# Revit family: M02
name_source: partatom
category: Verbindungsmittel
units: mm (PartAtom-declared; Revit-internal decimal feet)

## family parameters
Arbeitsebenenbasiert = Nein
Beim Laden mit Abzugskörper schneiden = Nein
Gemeinsam genutzt = Nein
Immer vertikal = Nein
OmniClass-Nummer = 23.25.10.27.11.21
OmniClass-Titel = Reinforcement Couplers

## types (9) — shared parameters
Endenbearbeitung 1 = Mit Gewinde
Endenbearbeitung 2 = Mit Gewinde
Hersteller = Stahlwerk Annahütte Max Aicher GmbH Co.KG
M02_Vis = Ja
Typenbild = M02.png
Typenkommentare = M02-Muffenstoß
URL = http//:www.annahuette.com

## per-type parameters (varying)
- M02-ø22/18: Außendurchmesser=40 mm  [stored 0.131234 ft]; Beschreibung=M02-ø22/8; Einfassung Stab 1=55 mm  [stored 0.180446 ft]; Einfassung Stab 2=50 mm  [stored 0.164042 ft]; Gesamtlänge=175 mm; Körper=1,00 kg; M03-Gewicht=1,22 kg; Modell=M02=TR 3102+TR2040; Nenndurchmesser_01 ø=22 mm  [stored 0.0721785 ft]; Nenndurchmesser_02 ø=18 mm  [stored 0.0590551 ft]; Pos_TR2040_01=95 mm; Pos_TR2040_02=95 mm; Pos_TR3102=73 mm; Stabgröße 1=SAS 670 - ø22; Stabgröße 2=SAS 670 - ø18; TR2040-G01=0,12 kg; TR2040-G02=0,10 kg; TR2040-L01=22 mm  [stored 0.0721785 ft]; TR2040-L02=22 mm  [stored 0.0721785 ft]; TR2040-Sw01=36 mm  [stored 0.11811 ft]; TR2040_Sw02=30 mm  [stored 0.0984252 ft]; TR3102-L=145 mm  [stored 0.475722 ft]; TR3102-L1=55 mm  [stored 0.180446 ft]; TR3102-L2=50 mm  [stored 0.164042 ft]; TR3102-d=40 mm  [stored 0.131234 ft]
- M02-ø25/22: Außendurchmesser=45 mm  [stored 0.147638 ft]; Beschreibung=M02-ø25/22; Einfassung Stab 1=60 mm  [stored 0.19685 ft]; Einfassung Stab 2=55 mm  [stored 0.180446 ft]; Gesamtlänge=190 mm; Körper=1,40 kg; M03-Gewicht=1,68 kg; Modell=M02=TR 3102+TR2040; Nenndurchmesser_01 ø=25 mm  [stored 0.082021 ft]; Nenndurchmesser_02 ø=22 mm  [stored 0.0721785 ft]; Pos_TR2040_01=102 mm  [stored 0.334646 ft]; Pos_TR2040_02=102 mm  [stored 0.334646 ft]; Pos_TR3102=80 mm  [stored 0.262467 ft]; Stabgröße 1=SAS 670 - ø25; Stabgröße 2=SAS 670 - ø22; TR2040-G01=0,16 kg; TR2040-G02=0,12 kg; TR2040-L01=22 mm  [stored 0.0721785 ft]; TR2040-L02=22 mm  [stored 0.0721785 ft]; TR2040-Sw01=41 mm  [stored 0.134514 ft]; TR2040_Sw02=36 mm  [stored 0.11811 ft]; TR3102-L=160 mm; TR3102-L1=60 mm  [stored 0.19685 ft]; TR3102-L2=55 mm  [stored 0.180446 ft]; TR3102-d=45 mm  [stored 0.147638 ft]
- M02-ø28/25: Außendurchmesser=50 mm  [stored 0.164042 ft]; Beschreibung=M02-ø28/25; Einfassung Stab 1=70 mm  [stored 0.229659 ft]; Einfassung Stab 2=60 mm  [stored 0.19685 ft]; Gesamtlänge=205 mm; Körper=2,00 kg; M03-Gewicht=2,42 kg; Modell=M02=TR 3102+TR2040; Nenndurchmesser_01 ø=28 mm  [stored 0.0918635 ft]; Nenndurchmesser_02 ø=25 mm  [stored 0.082021 ft]; Pos_TR2040_01=120 mm  [stored 0.393701 ft]; Pos_TR2040_02=112 mm; Pos_TR3102=90 mm  [stored 0.295276 ft]; Stabgröße 1=SAS 670 - ø28; Stabgröße 2=SAS 670 - ø25; TR2040-G01=0,26 kg; TR2040-G02=0,16 kg; TR2040-L01=30 mm  [stored 0.0984252 ft]; TR2040-L02=22 mm  [stored 0.0721785 ft]; TR2040-Sw01=46 mm  [stored 0.150919 ft]; TR2040_Sw02=41 mm  [stored 0.134514 ft]; TR3102-L=180 mm; TR3102-L1=70 mm  [stored 0.229659 ft]; TR3102-L2=60 mm  [stored 0.19685 ft]; TR3102-d=50 mm  [stored 0.164042 ft]
- M02-ø30/28: Außendurchmesser=55 mm  [stored 0.180446 ft]; Beschreibung=M02-ø30/28; Einfassung Stab 1=75 mm; Einfassung Stab 2=70 mm  [stored 0.229659 ft]; Gesamtlänge=225 mm; Körper=2,50 kg; M03-Gewicht=3,07 kg; Modell=M02=TR 3102+TR2040; Nenndurchmesser_01 ø=30 mm  [stored 0.0984252 ft]; Nenndurchmesser_02 ø=28 mm  [stored 0.0918635 ft]; Pos_TR2040_01=128 mm; Pos_TR2040_02=128 mm; Pos_TR3102=98 mm; Stabgröße 1=SAS 670 - ø30; Stabgröße 2=SAS 670 - ø28; TR2040-G01=0,31 kg; TR2040-G02=0,26 kg; TR2040-L01=30 mm  [stored 0.0984252 ft]; TR2040-L02=30 mm  [stored 0.0984252 ft]; TR2040-Sw01=50 mm  [stored 0.164042 ft]; TR2040_Sw02=46 mm  [stored 0.150919 ft]; TR3102-L=195 mm; TR3102-L1=75 mm; TR3102-L2=70 mm  [stored 0.229659 ft]; TR3102-d=55 mm  [stored 0.180446 ft]
- M02-ø35/30: Außendurchmesser=60 mm  [stored 0.19685 ft]; Beschreibung=M02-ø35/30; Einfassung Stab 1=85 mm  [stored 0.278871 ft]; Einfassung Stab 2=75 mm; Gesamtlänge=260 mm; Körper=3,00 kg; M03-Gewicht=3,78 kg; Modell=M02=TR 3102+TR2040; Nenndurchmesser_01 ø=35 mm  [stored 0.114829 ft]; Nenndurchmesser_02 ø=30 mm  [stored 0.0984252 ft]; Pos_TR2040_01=148 mm; Pos_TR2040_02=138 mm; Pos_TR3102=108 mm; Stabgröße 1=SAS 670 - ø35; Stabgröße 2=SAS 670 - ø30; TR2040-G01=0,47 kg; TR2040-G02=0,31 kg; TR2040-L01=40 mm  [stored 0.131234 ft]; TR2040-L02=30 mm  [stored 0.0984252 ft]; TR2040-Sw01=55 mm  [stored 0.180446 ft]; TR2040_Sw02=50 mm  [stored 0.164042 ft]; TR3102-L=215 mm; TR3102-L1=85 mm  [stored 0.278871 ft]; TR3102-L2=75 mm; TR3102-d=60 mm  [stored 0.19685 ft]
- M02-ø43/35: Außendurchmesser=80 mm  [stored 0.262467 ft]; Beschreibung=M02-ø43/35; Einfassung Stab 1=100 mm  [stored 0.328084 ft]; Einfassung Stab 2=85 mm  [stored 0.278871 ft]; Gesamtlänge=275 mm; Körper=5,50 kg; M03-Gewicht=6,97 kg; Modell=M02=TR 3102+TR2040; Nenndurchmesser_01 ø=43 mm  [stored 0.141076 ft]; Nenndurchmesser_02 ø=35 mm  [stored 0.114829 ft]; Pos_TR2040_01=175 mm; Pos_TR2040_02=165 mm; Pos_TR3102=125 mm  [stored 0.410105 ft]; Stabgröße 1=SAS 670 - ø43; Stabgröße 2=SAS 670 - ø35; TR2040-G01=1,00 kg; TR2040-G02=0,47 kg; TR2040-L01=50 mm  [stored 0.164042 ft]; TR2040-L02=40 mm  [stored 0.131234 ft]; TR2040-Sw01=70 mm  [stored 0.229659 ft]; TR2040_Sw02=55 mm  [stored 0.180446 ft]; TR3102-L=250 mm; TR3102-L1=100 mm  [stored 0.328084 ft]; TR3102-L2=85 mm  [stored 0.278871 ft]; TR3102-d=80 mm  [stored 0.262467 ft]
- M02-ø50/43: Außendurchmesser=85 mm  [stored 0.278871 ft]; Beschreibung=M02-ø50/43; Einfassung Stab 1=105 mm  [stored 0.344488 ft]; Einfassung Stab 2=100 mm  [stored 0.328084 ft]; Gesamtlänge=335 mm; Körper=7,68 kg; M03-Gewicht=9,94 kg; Modell=M02=TR3102+TR2040; Nenndurchmesser_01 ø=50 mm  [stored 0.164042 ft]; Nenndurchmesser_02 ø=43 mm  [stored 0.141076 ft]; Pos_TR2040_01=185 mm; Pos_TR2040_02=185 mm; Pos_TR3102=135 mm  [stored 0.442913 ft]; Stabgröße 1=SAS 670 - ø50; Stabgröße 2=SAS 670 - ø43; TR2040-G01=1,26 kg; TR2040-G02=1,00 kg; TR2040-L01=50 mm  [stored 0.164042 ft]; TR2040-L02=50 mm  [stored 0.164042 ft]; TR2040-Sw01=80 mm  [stored 0.262467 ft]; TR2040_Sw02=70 mm  [stored 0.229659 ft]; TR3102-L=270 mm; TR3102-L1=105 mm  [stored 0.344488 ft]; TR3102-L2=100 mm  [stored 0.328084 ft]; TR3102-d=85 mm  [stored 0.278871 ft]
- M02-ø57,5/50: Außendurchmesser=100 mm  [stored 0.328084 ft]; Beschreibung=M02-ø57,5/50; Einfassung Stab 1=125 mm  [stored 0.410105 ft]; Einfassung Stab 2=105 mm  [stored 0.344488 ft]; Gesamtlänge=350 mm; Körper=11,94 kg; M03-Gewicht=15,24 kg; Modell=M02=TR 3102+TR2040; Nenndurchmesser_01 ø=58 mm; Nenndurchmesser_02 ø=50 mm  [stored 0.164042 ft]; Pos_TR2040_01=208 mm; Pos_TR2040_02=198 mm; Pos_TR3102=148 mm; Stabgröße 1=SAS 670 - ø57,5; Stabgröße 2=SAS 670 - ø50; TR2040-G01=2,04 kg; TR2040-G02=1,26 kg; TR2040-L01=60 mm  [stored 0.19685 ft]; TR2040-L02=50 mm  [stored 0.164042 ft]; TR2040-Sw01=90 mm  [stored 0.295276 ft]; TR2040_Sw02=80 mm  [stored 0.262467 ft]; TR3102-L=295 mm; TR3102-L1=125 mm  [stored 0.410105 ft]; TR3102-L2=105 mm  [stored 0.344488 ft]; TR3102-d=100 mm  [stored 0.328084 ft]
- M02-ø63,5/57,5: Außendurchmesser=110 mm  [stored 0.360892 ft]; Beschreibung=M02-ø63,5/57,5; Einfassung Stab 1=130 mm  [stored 0.426509 ft]; Einfassung Stab 2=125 mm  [stored 0.410105 ft]; Gesamtlänge=405 mm; Körper=14,89 kg; M03-Gewicht=20,00 kg; Modell=M02=TR 3102+TR2040; Nenndurchmesser_01 ø=64 mm; Nenndurchmesser_02 ø=58 mm; Pos_TR2040_01=223 mm; Pos_TR2040_02=213 mm; Pos_TR3102=153 mm; Stabgröße 1=SAS 670 - ø63,5; Stabgröße 2=SAS 670 - ø57,5; TR2040-G01=3,07 kg; TR2040-G02=2,04 kg; TR2040-L01=70 mm  [stored 0.229659 ft]; TR2040-L02=60 mm  [stored 0.19685 ft]; TR2040-Sw01=100 mm  [stored 0.328084 ft]; TR2040_Sw02=90 mm  [stored 0.295276 ft]; TR3102-L=305 mm; TR3102-L1=130 mm  [stored 0.426509 ft]; TR3102-L2=125 mm  [stored 0.410105 ft]; TR3102-d=110 mm  [stored 0.360892 ft]

note: [stored X ft] marks values corroborated as IEEE doubles in the binary element streams (Revit-internal decimal feet)
